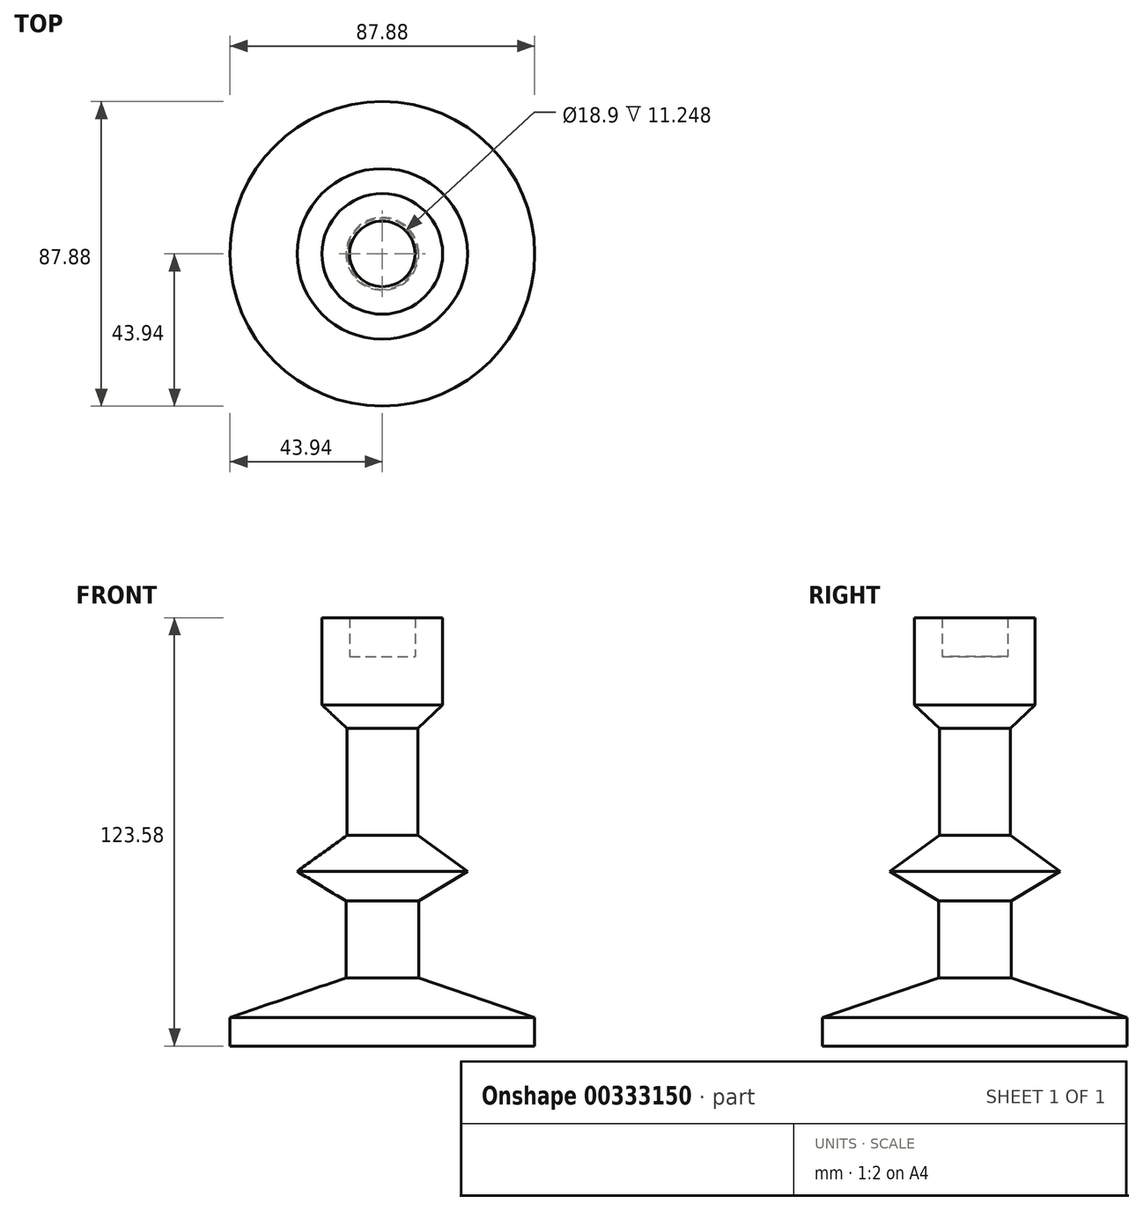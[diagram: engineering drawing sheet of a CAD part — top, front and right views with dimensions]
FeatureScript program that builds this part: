
annotation { "Feature Type Name" : "Feature", "Feature Type Description" : "" }
export const myFeature = defineFeature(function(context is Context, id is Id, definition is map)
    precondition{}
    {
        {
            var Q0;
            Q0=qCreatedBy(makeId("Front.planeOp"),FACE);
            var sketch = newSketch(context, id + "F0", { "sketchPlane" : qUnion([Q0])});
            skLineSegment(sketch, "E0", {"start": v(0, 56.24) * mm, "end": v(9.45, 56.24) * mm});
            skLineSegment(sketch, "E1", {"start": v(9.45, 56.24) * mm, "end": v(9.45, 67.5) * mm});
            skLineSegment(sketch, "E2", {"start": v(9.45, 67.5) * mm, "end": v(17.4, 67.5) * mm});
            skLineSegment(sketch, "E3", {"start": v(17.4, 67.5) * mm, "end": v(17.4, 42.3) * mm});
            skLineSegment(sketch, "E4", {"start": v(17.4, 42.3) * mm, "end": v(10.2, 35.55) * mm});
            skLineSegment(sketch, "E5", {"start": v(10.2, 35.55) * mm, "end": v(10.2, 4.65) * mm});
            skLineSegment(sketch, "E6", {"start": v(10.2, 4.65) * mm, "end": v(24.6, -5.7) * mm});
            skLineSegment(sketch, "E7", {"start": v(24.6, -5.7) * mm, "end": v(10.5, -14.25) * mm});
            skLineSegment(sketch, "E8", {"start": v(10.5, -14.25) * mm, "end": v(10.5, -36.45) * mm});
            skLineSegment(sketch, "E9", {"start": v(10.5, -36.45) * mm, "end": v(43.94, -47.84) * mm});
            skLineSegment(sketch, "E10", {"start": v(43.94, -47.84) * mm, "end": v(43.94, -56.1) * mm});
            skLineSegment(sketch, "E11", {"start": v(43.94, -56.1) * mm, "end": v(0, -56.1) * mm});
            skLineSegment(sketch, "E12", {"start": v(0, -56.1) * mm, "end": v(0, 56.24) * mm});
            skSolve(sketch);
        }
        {
            var Q0;
            Q0 = qSketchRegion(id + "F0", true);
            var Q1;
            Q1=sQuery(id+"F0.wireOp",EDGE,"E12");
            revolve(context, id + "F1", {"entities" : qUnion([Q0]), "axis" : qUnion([Q1]), "revolveType" : RevolveType.FULL});
        }
        {
            var Q0;
            Q0=qCreatedBy(makeId("Top.planeOp"),FACE);
            var sketch = newSketch(context, id + "F2", { "sketchPlane" : qUnion([Q0])});
            skCircle(sketch, "E13", {"center": v(0, 0) * mm, "radius": 33.67 * mm});
            skSolve(sketch);
        }
        {
            var Q0;
            Q0=qCreatedBy(makeId("Front.planeOp"),FACE);
            var sketch = newSketch(context, id + "F3", { "sketchPlane" : qUnion([Q0])});
            skCircle(sketch, "E14", {"center": v(26.67, -41.82) * mm, "radius": 4.09 * mm});
            skSolve(sketch);
        }
        {
            var Q0;
            Q0=sQuery(id+"F3.wireOp",EDGE,"E14");
            var Q1;
            Q1=sQuery(id+"F2.wireOp",EDGE,"E13");
            revolve(context, id + "F4", {"bodyType" : ToolBodyType.SURFACE, "surfaceEntities" : qUnion([Q0]), "axis" : qUnion([Q1]), "revolveType" : RevolveType.FULL});
        }
        {
            var Q0;
            Q0=qCreatedBy(makeId("Front.planeOp"),FACE);
            var sketch = newSketch(context, id + "F5", { "sketchPlane" : qUnion([Q0])});
            skCircle(sketch, "E15", {"center": v(36.41, -45.35) * mm, "radius": 3.32 * mm});
            skSolve(sketch);
        }
        {
            var Q0;
            Q0=sQuery(id+"F5.wireOp",EDGE,"E15");
            var Q1;
            Q1=makeQuery(id+"F4.opRevolve","SWEPT_FACE",FACE,{"disambiguationData":[OSD([sQuery(id+"F3.wireOp",EDGE,"E14")])]});
            revolve(context, id + "F6", {"bodyType" : ToolBodyType.SURFACE, "surfaceEntities" : qUnion([Q0]), "axis" : qUnion([Q1]), "revolveType" : RevolveType.FULL});
        }
    });
